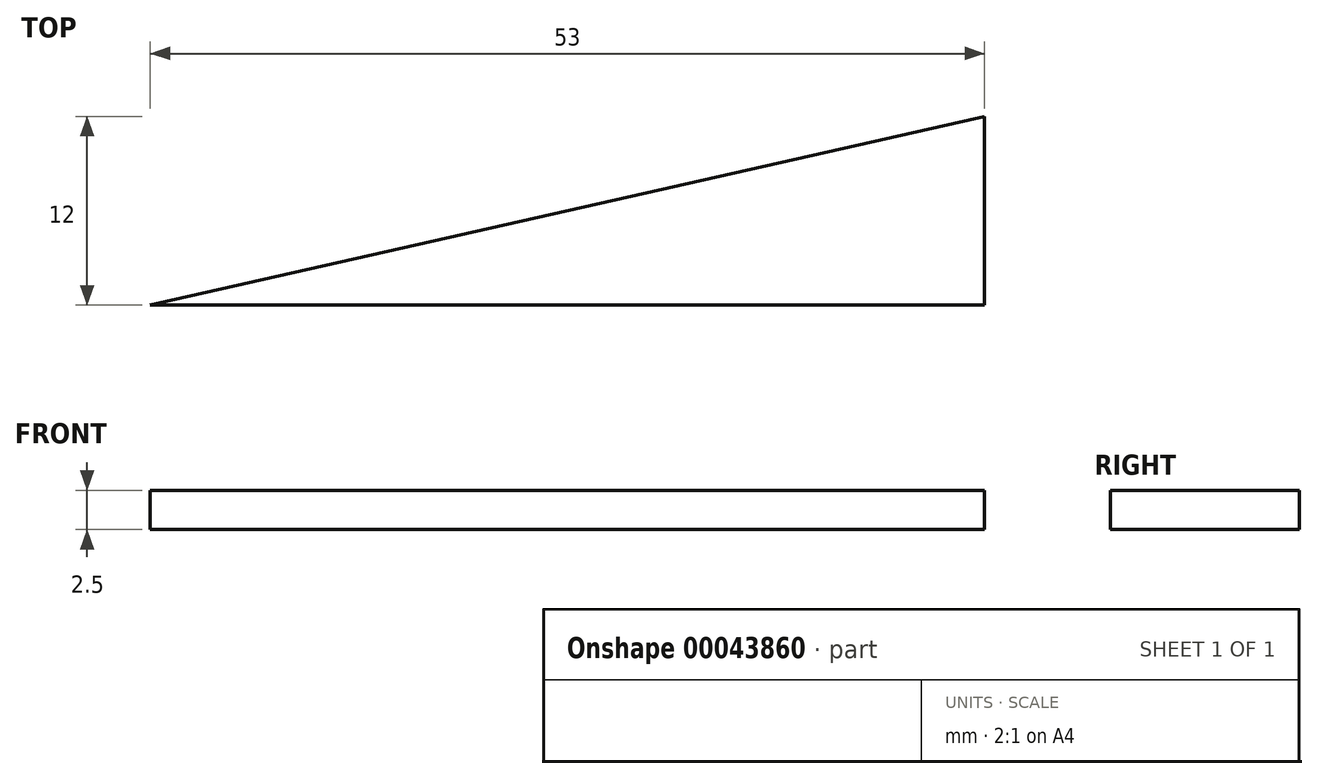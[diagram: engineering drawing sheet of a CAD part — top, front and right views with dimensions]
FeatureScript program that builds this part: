
annotation { "Feature Type Name" : "Feature", "Feature Type Description" : "" }
export const myFeature = defineFeature(function(context is Context, id is Id, definition is map)
    precondition{}
    {
        {
            var Q0;
            Q0=qCreatedBy(makeId("Top.planeOp"),FACE);
            var sketch = newSketch(context, id + "F0", { "sketchPlane" : qUnion([Q0])});
            skLineSegment(sketch, "E0", {"start": v(0, 0) * mm, "end": v(-53, 0) * mm});
            skLineSegment(sketch, "E1", {"start": v(-53, 0) * mm, "end": v(0, 12) * mm});
            skLineSegment(sketch, "E2", {"start": v(0, 12) * mm, "end": v(0, 0) * mm});
            skSolve(sketch);
        }
        {
            var Q0;
            Q0 = qSketchRegion(id + "F0", true);
            extrude(context, id + "F1", {"entities" : qUnion([Q0]), "depth" : 2.5 * mm, "offsetDistance" : 25 * mm});
        }
    });
